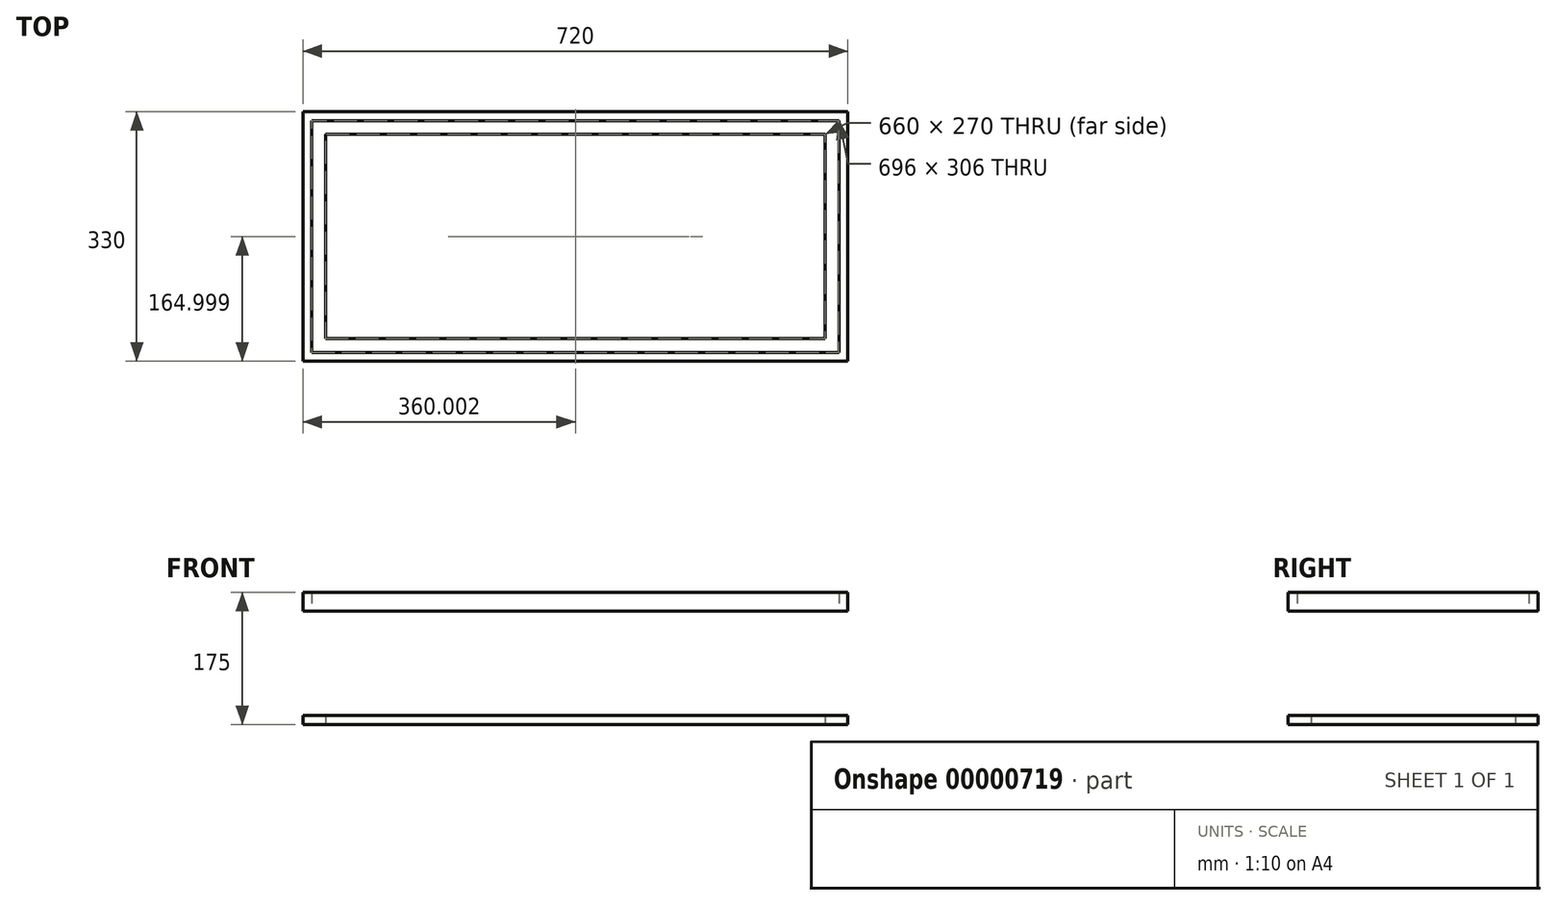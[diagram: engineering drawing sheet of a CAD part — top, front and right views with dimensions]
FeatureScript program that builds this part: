
annotation { "Feature Type Name" : "Feature", "Feature Type Description" : "" }
export const myFeature = defineFeature(function(context is Context, id is Id, definition is map)
    precondition{}
    {
        {
            var Q0;
            Q0=qCreatedBy(makeId("Top.planeOp"),FACE);
            cPlane(context, id + "F0", {"entities" : qUnion([Q0]), "cplaneType" : CPlaneType.OFFSET, "offset" : 150 * mm, "width" : 150 * mm, "height" : 150 * mm});
        }
        {
            var Q0;
            Q0=qCreatedBy(makeId("Top.planeOp"),FACE);
            var sketch = newSketch(context, id + "F1", { "sketchPlane" : qUnion([Q0])});
            skLineSegment(sketch, "E0.bottom", {"start": v(-499.83, 152.1) * mm, "end": v(220.17, 152.1) * mm});
            skLineSegment(sketch, "E0.top", {"start": v(-499.83, -177.9) * mm, "end": v(220.17, -177.9) * mm});
            skLineSegment(sketch, "E0.left", {"start": v(-499.83, 152.1) * mm, "end": v(-499.83, -177.9) * mm});
            skLineSegment(sketch, "E0.right", {"start": v(220.17, 152.1) * mm, "end": v(220.17, -177.9) * mm});
            skLineSegment(sketch, "E1.bottom", {"start": v(-469.83, 122.1) * mm, "end": v(190.17, 122.1) * mm});
            skLineSegment(sketch, "E1.top", {"start": v(-469.83, -147.9) * mm, "end": v(190.17, -147.9) * mm});
            skLineSegment(sketch, "E1.left", {"start": v(-469.83, 122.1) * mm, "end": v(-469.83, -147.9) * mm});
            skLineSegment(sketch, "E1.right", {"start": v(190.17, 122.1) * mm, "end": v(190.17, -147.9) * mm});
            skSolve(sketch);
        }
        {
            var Q0;
            Q0=makeQuery(id+"F1.imprint","IMPRINT",FACE,{"disambiguationData":[TD([[makeQuery(id+"F1.imprint","IMPRINT",EDGE,{"derivedFrom":sQuery(id+"F1.wireOp",EDGE,"E0.bottom")}),-1.0]])]});
            extrude(context, id + "F2", {"entities" : qUnion([Q0]), "depth" : 12 * mm});
        }
        {
            var Q0;
            Q0=qCreatedBy(id+"F0.planeOp",FACE);
            var sketch = newSketch(context, id + "F3", { "sketchPlane" : qUnion([Q0])});
            skLineSegment(sketch, "E2.bottom", {"start": v(-499.83, 152.1) * mm, "end": v(220.17, 152.1) * mm});
            skLineSegment(sketch, "E2.top", {"start": v(-499.83, -177.9) * mm, "end": v(220.17, -177.9) * mm});
            skLineSegment(sketch, "E2.left", {"start": v(-499.83, 152.1) * mm, "end": v(-499.83, -177.9) * mm});
            skLineSegment(sketch, "E2.right", {"start": v(220.17, 152.1) * mm, "end": v(220.17, -177.9) * mm});
            skLineSegment(sketch, "E3.bottom", {"start": v(208.17, -165.9) * mm, "end": v(-487.83, -165.9) * mm});
            skLineSegment(sketch, "E3.top", {"start": v(208.17, 140.1) * mm, "end": v(-487.83, 140.1) * mm});
            skLineSegment(sketch, "E3.left", {"start": v(208.17, -165.9) * mm, "end": v(208.17, 140.1) * mm});
            skLineSegment(sketch, "E3.right", {"start": v(-487.83, -165.9) * mm, "end": v(-487.83, 140.1) * mm});
            skSolve(sketch);
        }
        {
            var Q0;
            Q0=makeQuery(id+"F3.imprint","IMPRINT",FACE,{"disambiguationData":[TD([[makeQuery(id+"F3.imprint","IMPRINT",EDGE,{"derivedFrom":sQuery(id+"F3.wireOp",EDGE,"E2.bottom")}),-1.0]])]});
            extrude(context, id + "F4", {"entities" : qUnion([Q0]), "depth" : 25 * mm});
        }
    });
